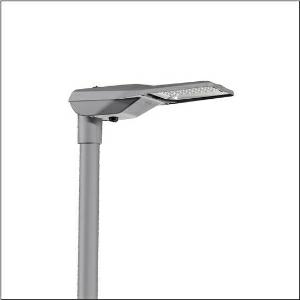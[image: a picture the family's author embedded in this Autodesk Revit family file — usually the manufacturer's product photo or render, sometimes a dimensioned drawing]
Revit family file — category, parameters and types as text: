
# Revit family: streetlight_sl_21_mini___st1_5a_5xe2p43t08hb_3154
name_source: partatom
category: Lighting Fixtures
units: mm (PartAtom-declared; Revit-internal decimal feet)

## family parameters
Cut with Voids When Loaded = No
Host = Face
Light Source = No
Part Type = Normal
Room Calculation Point = No
Round Connector Dimension = Use Diameter
Shared = No

## types (1)
- --- (1 x LED, 9260 lm, 66 W, 4000K)
    Apparent Load = 66 VA
    CIE Flux Codes = 22 53 95 100 100
    Color Rendering = 70
    Color Temperature = 4000K
    Default Elevation = 1800 mm
    Description = Streetlight SL 21 mini, mast luminaire, primary light control with lens, of PMMA, primary optical cover: cover, of toughened safety glass, transparent, light distribution: ST1.5a, light emission: direct distribution, primary light characteristic: asymmetric, installation type: side-entry, post-top, LED, High Power LED, rated luminous flux: 9.260lm, luminous efficacy: 140lm/W, light colour: 740, colour temperature: 4000K, control gear: D4i, control: overheat protection, constant luminous flux control, time-dependent luminous flux control, flexible luminous flux parameterisation, pre-setting: logarithmic dimming characteristic, mains connection: 220..240V, AC, 50/60Hz, start of lifetime: 66W, end of service life: 69W, reduction: 30W, luminaire housing, of diecast aluminium, powder-coated, SITECO metallic grey (DB 702S), corrosivity category C5 high according to DIN EN ISO 12944, please order mast flange separately, inclination adjustable: 0°, 5°, 10°, 15°, sealing non-destructively replaceable, multi-level sealing system, length: 628mm, width: 235mm, height: 110mm, mast flange for spigot size: 42mm (side-entry): 5XC10008XM4, 60/48mm (side-entry/post-top): 5XC10108XM2, 76/60mm (side-entry/post-top): 5XC10108XM1, mounting height: 4..8m, Smart Interface below and above, protection rating (complete): IP66, insulation class (complete): insulation class II (safety insulation), certification: CE, ENEC, ENEC+, VDE, impact resistance: IK10, permissible operating ambient temperature for outdoor applications: -40..+50°C, standard-compliant lighting for roads and squares, packaging unit: 1 piece

Light Distribution: ST1.5a
    Height = 110 mm
    Lamp = 1 x LED
    Lamp Light Flux = 9260 lm
    Lamp Power = 66 W
    Lamp count = 1
    Length = 625 mm
    Luminous efficacy = 140 lm/W
    Manufacturer = Siteco
    ModVariant = No
    Model = 5XE2P43T08HB
    Number of Poles = 1
    OnlyDefault = Yes
    Power Factor = 1
    Product Name = Streetlight SL 21 mini | ST1.5a
    Product group = mast luminaire | pylon top
    ProductGroupID = 6100
    Protection Class = Protection class II
    Protection Degree = IP 66
    RLX_Detail_Level = 1
    RLX_Emergency_Light_Flux = 0 lm
    RLX_Emergency_Type = 0
    RLX_Emergency_Type_DB = No
    RlxData = <blob elided: 29781 chars, md5=c12f2ee0>
    Socket = socket
    Standby Power = 0 W
    System Light Flux = 9260 lm
    System Power = 66 W
    Type Comments = factory setting: luminous flux: 100 % | dim-lin: 254 | 670 mA
    Type Image = l_1003514.jpg
    URL = http://relux.com
    VarID = @adj_174941
    Voltage = 0 V
    Weight = 0.00 kg
    Width = 234 mm

## geometry (parser evidence)
native form markers: Blend x4, Sweep x10
no freeform markers — native parametric forms only
